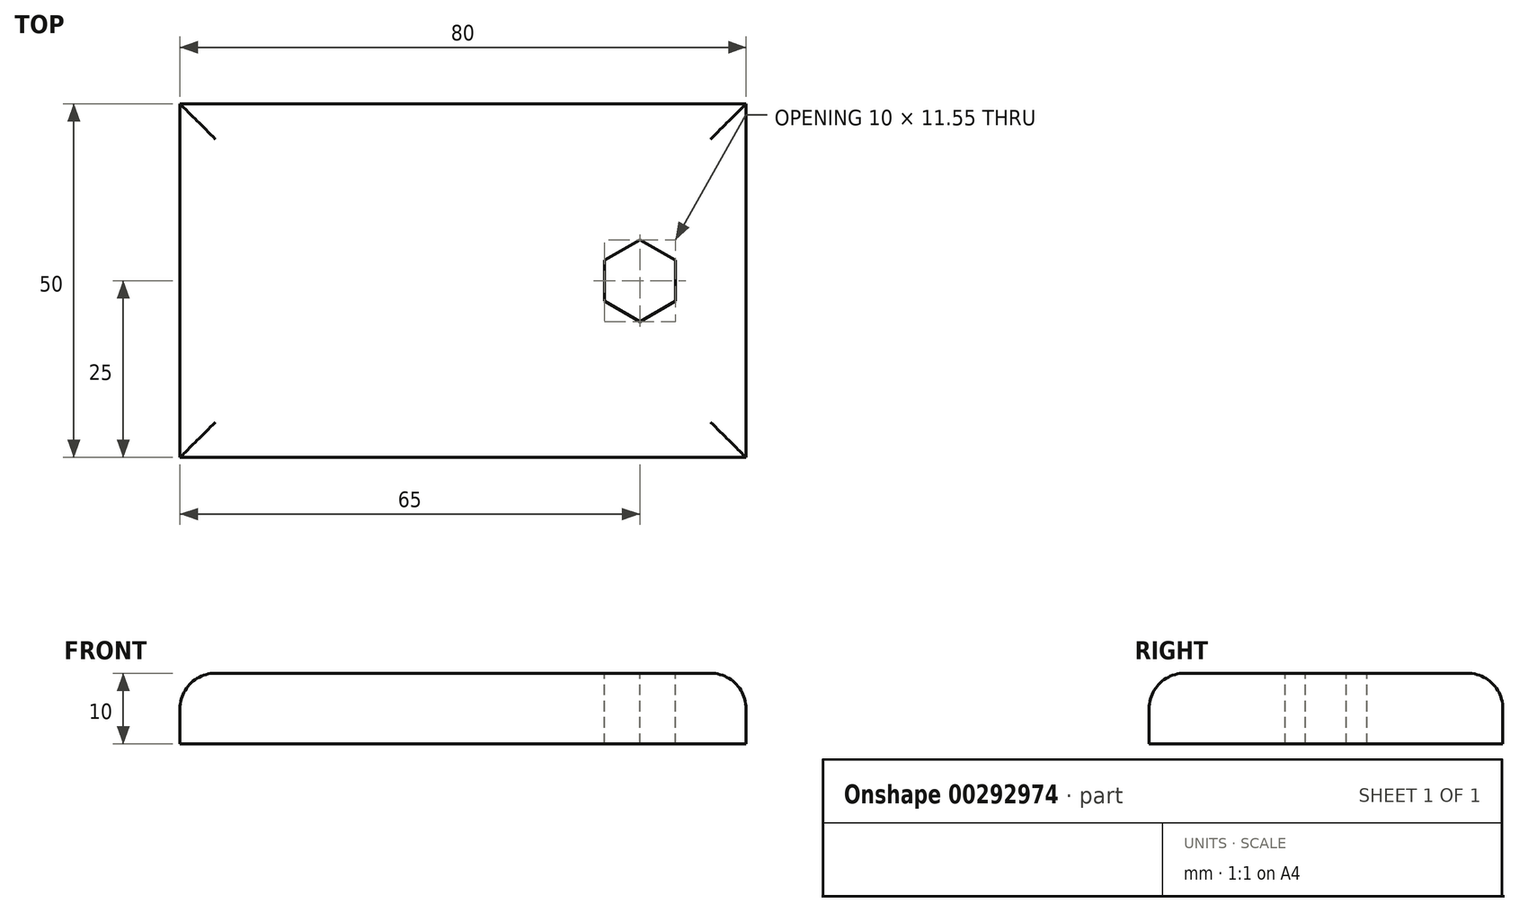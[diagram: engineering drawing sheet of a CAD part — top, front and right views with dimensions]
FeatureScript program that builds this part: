
annotation { "Feature Type Name" : "Feature", "Feature Type Description" : "" }
export const myFeature = defineFeature(function(context is Context, id is Id, definition is map)
    precondition{}
    {
        {
            var Q0;
            Q0=qCreatedBy(makeId("Top.planeOp"),FACE);
            var sketch = newSketch(context, id + "F0", { "sketchPlane" : qUnion([Q0])});
            skLineSegment(sketch, "E0.bottom", {"start": v(-40, -25) * mm, "end": v(40, -25) * mm});
            skLineSegment(sketch, "E0.top", {"start": v(-40, 25) * mm, "end": v(40, 25) * mm});
            skLineSegment(sketch, "E0.left", {"start": v(-40, -25) * mm, "end": v(-40, 25) * mm});
            skLineSegment(sketch, "E0.right", {"start": v(40, -25) * mm, "end": v(40, 25) * mm});
            skPoint(sketch, "E1", {"position": v(0, -25) * mm});
            skPoint(sketch, "E2", {"position": v(-40, 0) * mm});
            skSolve(sketch);
        }
        {
            var Q0;
            Q0=makeQuery(id+"F0.imprint","IMPRINT",FACE,{"disambiguationData":[TD([[makeQuery(id+"F0.imprint","IMPRINT",EDGE,{"derivedFrom":sQuery(id+"F0.wireOp",EDGE,"E0.bottom")}),1.0]])]});
            extrude(context, id + "F1", {"entities" : qUnion([Q0]), "depth" : 10 * mm});
        }
        {
            var Q0;
            Q0=makeQuery(id+"F1.opExtrude","CAP_FACE",FACE,{"disambiguationData":[OSD([sQuery(id+"F0.wireOp",EDGE,"E0.bottom"),sQuery(id+"F0.wireOp",EDGE,"E0.top"),sQuery(id+"F0.wireOp",EDGE,"E0.left"),sQuery(id+"F0.wireOp",EDGE,"E0.right")])],"isStart":false});
            var sketch = newSketch(context, id + "F2", { "sketchPlane" : qUnion([Q0])});
            skCircle(sketch, "E3.cCircle", {"center": v(25, 0) * mm, "radius": 5.77 * mm, "construction": true});
            skLineSegment(sketch, "E3.0", {"start": v(30, -2.89) * mm, "end": v(25, -5.77) * mm});
            skLineSegment(sketch, "E3.1", {"start": v(25, -5.77) * mm, "end": v(20, -2.89) * mm});
            skLineSegment(sketch, "E3.2", {"start": v(20, -2.89) * mm, "end": v(20, 2.89) * mm});
            skLineSegment(sketch, "E3.3", {"start": v(20, 2.89) * mm, "end": v(25, 5.77) * mm});
            skLineSegment(sketch, "E3.4", {"start": v(25, 5.77) * mm, "end": v(30, 2.89) * mm});
            skLineSegment(sketch, "E3.5", {"start": v(30, 2.89) * mm, "end": v(30, -2.89) * mm});
            skSolve(sketch);
        }
        {
            var Q0;
            Q0=makeQuery(id+"F2.imprint","IMPRINT",FACE,{"disambiguationData":[TD([[makeQuery(id+"F2.imprint","IMPRINT",EDGE,{"derivedFrom":sQuery(id+"F2.wireOp",EDGE,"E3.0")}),-1.0]])]});
            extrude(context, id + "F3", {"entities" : qUnion([Q0]), "operationType" : NewBodyOperationType.REMOVE, "oppositeDirection" : true, "depth" : 15 * mm});
        }
        {
            var Q0;
            Q0=makeQuery(id+"F1.opExtrude","CAP_EDGE",EDGE,{"disambiguationData":[OSD([sQuery(id+"F0.wireOp",EDGE,"E0.bottom")])],"isStart":false});
            var Q1;
            Q1=makeQuery(id+"F1.opExtrude","CAP_EDGE",EDGE,{"disambiguationData":[OSD([sQuery(id+"F0.wireOp",EDGE,"E0.right")])],"isStart":false});
            var Q2;
            Q2=makeQuery(id+"F1.opExtrude","CAP_EDGE",EDGE,{"disambiguationData":[OSD([sQuery(id+"F0.wireOp",EDGE,"E0.top")])],"isStart":false});
            var Q3;
            Q3=makeQuery(id+"F1.opExtrude","CAP_EDGE",EDGE,{"disambiguationData":[OSD([sQuery(id+"F0.wireOp",EDGE,"E0.left")])],"isStart":false});
            fillet(context, id + "F4", {"entities" : qUnion([Q0, Q1, Q2, Q3]), "radius" : 5 * mm, "tangentPropagation" : true, "allowEdgeOverflow" : false});
        }
    });
